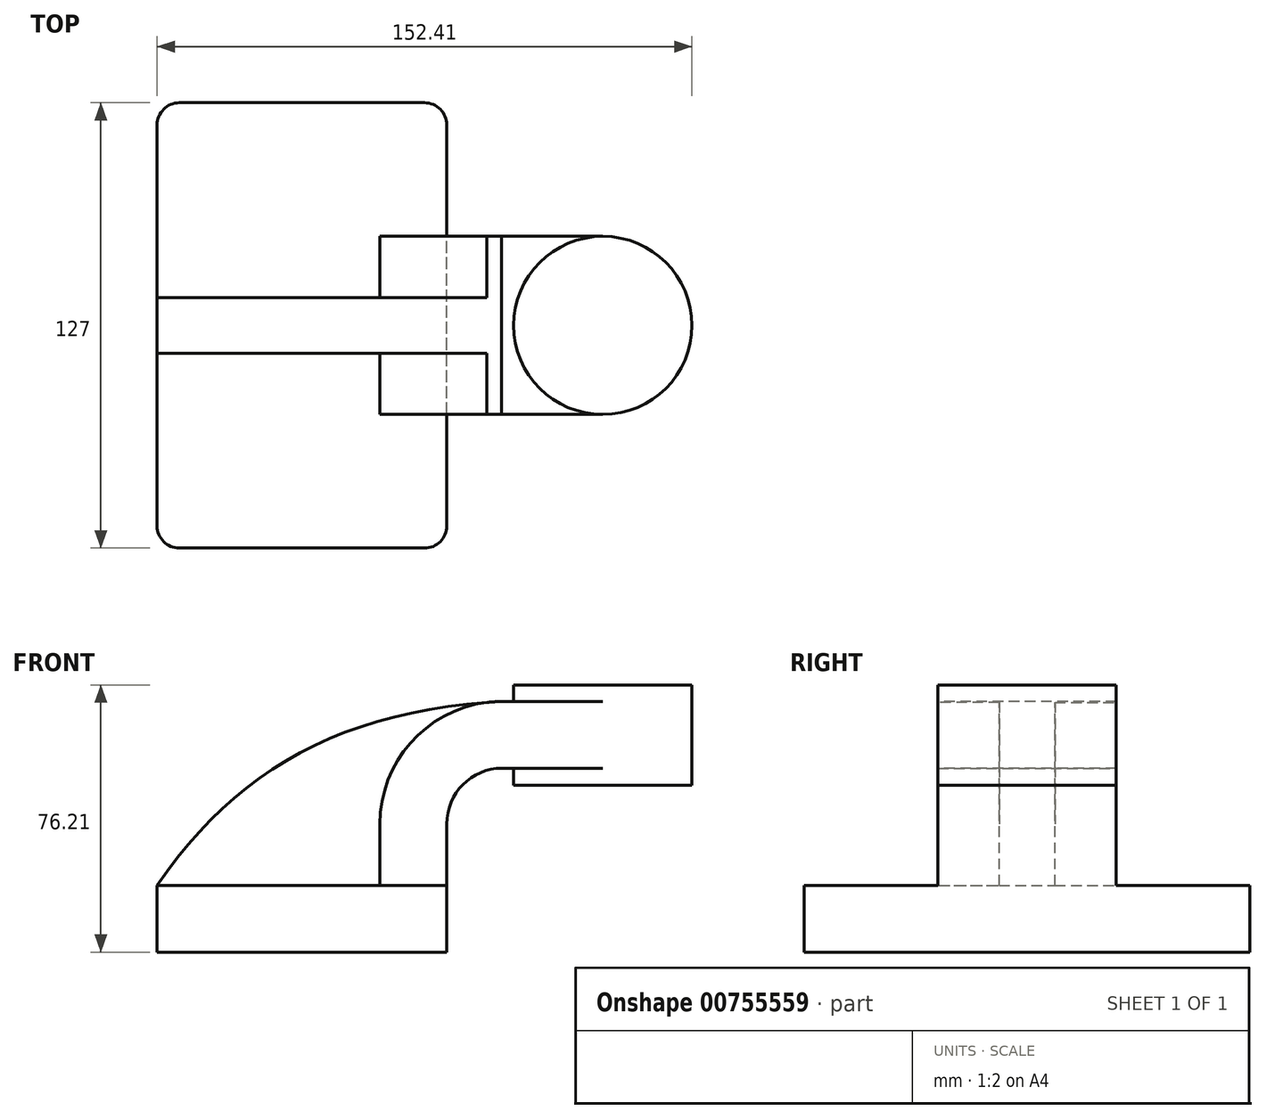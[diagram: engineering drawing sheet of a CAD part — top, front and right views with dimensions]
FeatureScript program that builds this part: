
annotation { "Feature Type Name" : "Feature", "Feature Type Description" : "" }
export const myFeature = defineFeature(function(context is Context, id is Id, definition is map)
    precondition{}
    {
        {
            var Q0;
            Q0=qCreatedBy(makeId("Front.planeOp"),FACE);
            var sketch = newSketch(context, id + "F0", { "sketchPlane" : qUnion([Q0])});
            skLineSegment(sketch, "E0.bottom", {"start": v(-41.28, 9.52) * mm, "end": v(41.27, 9.53) * mm});
            skLineSegment(sketch, "E0.top", {"start": v(-41.28, -9.53) * mm, "end": v(41.28, -9.53) * mm});
            skLineSegment(sketch, "E0.left", {"start": v(-41.28, 9.52) * mm, "end": v(-41.27, -9.53) * mm});
            skLineSegment(sketch, "E0.right", {"start": v(41.28, 9.53) * mm, "end": v(41.28, -9.52) * mm});
            skPoint(sketch, "E0.middle", {"position": v(0, 0) * mm});
            skLineSegment(sketch, "E1.bottom", {"start": v(60.33, 38.1) * mm, "end": v(111.12, 38.1) * mm});
            skLineSegment(sketch, "E1.top", {"start": v(60.32, 66.68) * mm, "end": v(111.12, 66.68) * mm});
            skLineSegment(sketch, "E1.left", {"start": v(60.32, 38.1) * mm, "end": v(60.32, 66.68) * mm});
            skLineSegment(sketch, "E1.right", {"start": v(111.12, 38.1) * mm, "end": v(111.12, 66.68) * mm});
            skPoint(sketch, "E1.middle", {"position": v(85.72, 52.39) * mm});
            skLineSegment(sketch, "E2", {"start": v(41.27, 9.53) * mm, "end": v(41.27, 27.05) * mm});
            skArc(sketch, "E3", {"start": v(41.27, 27.05) * mm, "mid": v(45.87, 38.22) * mm, "end": v(57, 42.93) * mm});
            skLineSegment(sketch, "E4", {"start": v(57, 42.93) * mm, "end": v(85.72, 42.93) * mm});
            skLineSegment(sketch, "E5.0", {"start": v(56.92, 61.98) * mm, "end": v(85.72, 61.98) * mm});
            skArc(sketch, "E5.1", {"start": v(22.22, 27.05) * mm, "mid": v(32.37, 51.67) * mm, "end": v(56.92, 61.98) * mm});
            skLineSegment(sketch, "E5.2", {"start": v(22.22, 9.53) * mm, "end": v(22.22, 27.05) * mm});
            skFitSpline(sketch, "E6", {"points": [v(-41.28, 9.53) * mm, v(56.92, 61.98) * mm], "startDerivative": vector(67.35, 98.12) * mm, "endDerivative": vector(138.4, 7.99) * mm});
            skPoint(sketch, "E7", {"position": v(85.72, 66.68) * mm});
            skLineSegment(sketch, "E8", {"start": v(85.72, 66.68) * mm, "end": v(85.72, 38.1) * mm});
            skSolve(sketch);
        }
        {
            var Q0;
            Q0=makeQuery(id+"F0.imprint","IMPRINT",FACE,{"disambiguationData":[TD([[makeQuery(id+"F0.imprint","IMPRINT",EDGE,{"derivedFrom":sQuery(id+"F0.wireOp",EDGE,"E0.top")}),1.0]])]});
            extrude(context, id + "F1", {"entities" : qUnion([Q0]), "endBound" : BoundingType.SYMMETRIC, "depth" : 127 * mm, "offsetDistance" : 25.4 * mm});
        }
        {
            var Q0;
            {var subQ1=sQuery(id+"F0.wireOp",EDGE,"E2");Q0=makeQuery(id+"F0.imprint","IMPRINT",FACE,{"disambiguationData":[TD([[makeQuery(id+"F0.imprint","IMPRINT",EDGE,{"derivedFrom":subQ1}),1.0]])]});}
            var Q1;
            {var subQ5=sQuery(id+"F0.wireOp",EDGE,"9bU2WvLI-HjLk-uA1j-yy2V-oizjqRQsUKOy");Q1=makeQuery(id+"F0.imprint","IMPRINT",FACE,{"disambiguationData":[TD([[makeQuery(id+"F0.imprint","IMPRINT",EDGE,{"derivedFrom":subQ5}),-1.0]])]});}
            var Q2;
            {var subQ0=sQuery(id+"F0.wireOp",EDGE,"E4");var subQ1=sQuery(id+"F0.wireOp",EDGE,"E1.left");var subQ2=makeQuery(id+"F0.imprint","INTERSECT",VERTEX,{"derivedFrom":[subQ1,subQ0]});Q2=makeQuery(id+"F0.imprint","IMPRINT",FACE,{"disambiguationData":[TD([[makeQuery(id+"F0.imprint","IMPRINT",EDGE,{"disambiguationData":[TD([[subQ2,-1.0]])],"derivedFrom":subQ1}),-1.0]])]});}
            extrude(context, id + "F2", {"entities" : qUnion([Q0, Q1, Q2]), "endBound" : BoundingType.SYMMETRIC, "depth" : 50.8 * mm, "offsetDistance" : 25.4 * mm});
        }
        {
            var Q0;
            {var subQ3=sQuery(id+"F0.wireOp",EDGE,"E5.2");Q0=makeQuery(id+"F0.imprint","IMPRINT",FACE,{"disambiguationData":[TD([[makeQuery(id+"F0.imprint","IMPRINT",EDGE,{"derivedFrom":subQ3}),1.0]])]});}
            extrude(context, id + "F3", {"entities" : qUnion([Q0]), "operationType" : NewBodyOperationType.ADD, "endBound" : BoundingType.SYMMETRIC, "depth" : 15.88 * mm, "offsetDistance" : 25.4 * mm});
        }
        {
            var Q0;
            {var subQ4=sQuery(id+"F0.wireOp",EDGE,"E1.right");Q0=makeQuery(id+"F0.imprint","IMPRINT",FACE,{"disambiguationData":[TD([[makeQuery(id+"F0.imprint","IMPRINT",EDGE,{"derivedFrom":subQ4}),1.0]])]});}
            var Q1;
            Q1=sQuery(id+"F0.wireOp",EDGE,"E8");
            revolve(context, id + "F4", {"operationType" : NewBodyOperationType.ADD, "surfaceOperationType" : NewSurfaceOperationType.NEW, "entities" : qUnion([Q0]), "axis" : qUnion([Q1]), "revolveType" : RevolveType.FULL});
        }
        {
            var Q0;
            Q0=makeQuery(id+"F1.opExtrude","CAP_EDGE",EDGE,{"disambiguationData":[OSD([sQuery(id+"F0.wireOp",EDGE,"E0.left")])],"isStart":false});
            var Q1;
            Q1=makeQuery(id+"F1.opExtrude","CAP_EDGE",EDGE,{"disambiguationData":[OSD([sQuery(id+"F0.wireOp",EDGE,"E0.right")])],"isStart":false});
            var Q2;
            Q2=makeQuery(id+"F1.opExtrude","CAP_EDGE",EDGE,{"disambiguationData":[OSD([sQuery(id+"F0.wireOp",EDGE,"E0.right")])],"isStart":true});
            var Q3;
            Q3=makeQuery(id+"F1.opExtrude","CAP_EDGE",EDGE,{"disambiguationData":[OSD([sQuery(id+"F0.wireOp",EDGE,"E0.left")])],"isStart":true});
            fillet(context, id + "F5", {"entities" : qUnion([Q0, Q1, Q2, Q3]), "radius" : 6.35 * mm, "tangentPropagation" : true, "allowEdgeOverflow" : false});
        }
    });
